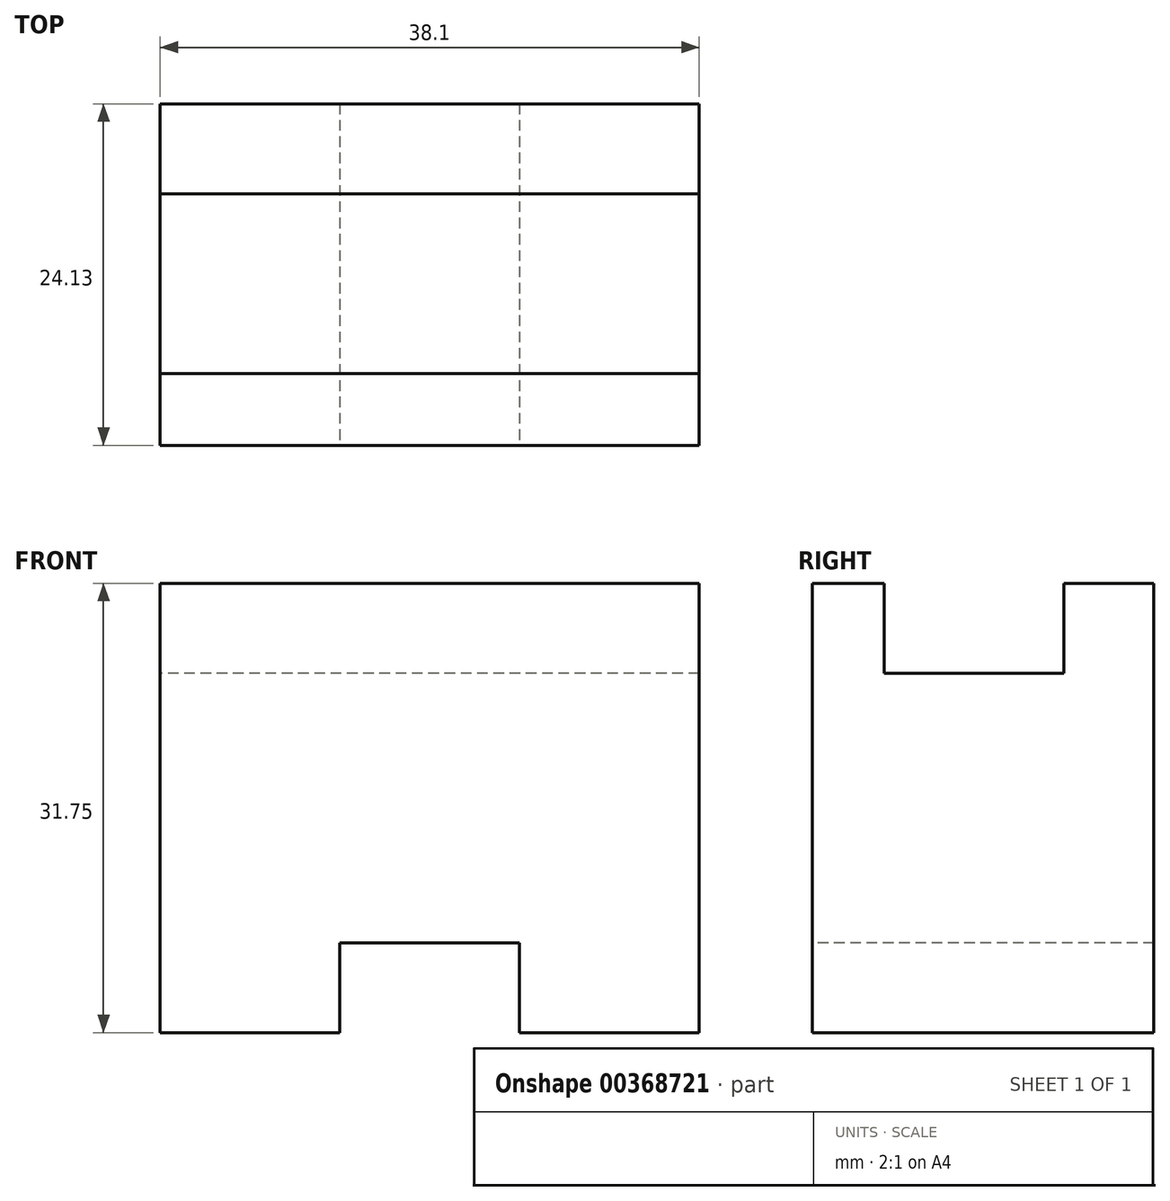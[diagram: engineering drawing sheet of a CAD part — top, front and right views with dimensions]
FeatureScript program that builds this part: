
annotation { "Feature Type Name" : "Feature", "Feature Type Description" : "" }
export const myFeature = defineFeature(function(context is Context, id is Id, definition is map)
    precondition{}
    {
        {
            var Q0;
            Q0=qCreatedBy(makeId("Right.planeOp"),FACE);
            var sketch = newSketch(context, id + "F0", { "sketchPlane" : qUnion([Q0])});
            skLineSegment(sketch, "E0", {"start": v(0, 0) * mm, "end": v(12.7, 0) * mm});
            skLineSegment(sketch, "E1", {"start": v(12.7, 0) * mm, "end": v(12.7, 31.75) * mm});
            skLineSegment(sketch, "E2", {"start": v(12.7, 31.75) * mm, "end": v(6.35, 31.75) * mm});
            skLineSegment(sketch, "E3", {"start": v(6.35, 31.75) * mm, "end": v(6.35, 25.4) * mm});
            skLineSegment(sketch, "E4", {"start": v(6.35, 25.4) * mm, "end": v(-6.35, 25.4) * mm});
            skLineSegment(sketch, "E5", {"start": v(-6.35, 25.4) * mm, "end": v(-6.35, 31.75) * mm});
            skLineSegment(sketch, "E6", {"start": v(-6.35, 31.75) * mm, "end": v(-11.43, 31.75) * mm});
            skLineSegment(sketch, "E7", {"start": v(-11.43, 31.75) * mm, "end": v(-11.43, 0) * mm});
            skLineSegment(sketch, "E8", {"start": v(0, 0) * mm, "end": v(-11.43, 0) * mm});
            skSolve(sketch);
        }
        {
            var Q0;
            Q0 = qSketchRegion(id + "F0", true);
            extrude(context, id + "F1", {"entities" : qUnion([Q0]), "depth" : 38.1 * mm});
        }
        {
            var Q0;
            Q0=makeQuery(id+"F1.opExtrude","SWEPT_FACE",FACE,{"disambiguationData":[OSD([sQuery(id+"F0.wireOp",EDGE,"E7")])]});
            var sketch = newSketch(context, id + "F2", { "sketchPlane" : qUnion([Q0])});
            skLineSegment(sketch, "E9", {"start": v(0, 0) * mm, "end": v(12.7, 0) * mm});
            skLineSegment(sketch, "E10", {"start": v(12.7, 0) * mm, "end": v(12.7, 6.35) * mm});
            skLineSegment(sketch, "E11", {"start": v(12.7, 6.35) * mm, "end": v(25.4, 6.35) * mm});
            skLineSegment(sketch, "E12", {"start": v(25.4, 6.35) * mm, "end": v(25.4, 0) * mm});
            skLineSegment(sketch, "E13", {"start": v(25.4, 0) * mm, "end": v(12.7, 0) * mm});
            skSolve(sketch);
        }
        {
            var Q0;
            Q0 = qSketchRegion(id + "F2", true);
            extrude(context, id + "F3", {"entities" : qUnion([Q0]), "operationType" : NewBodyOperationType.REMOVE, "oppositeDirection" : true, "depth" : 25.4 * mm});
        }
    });
